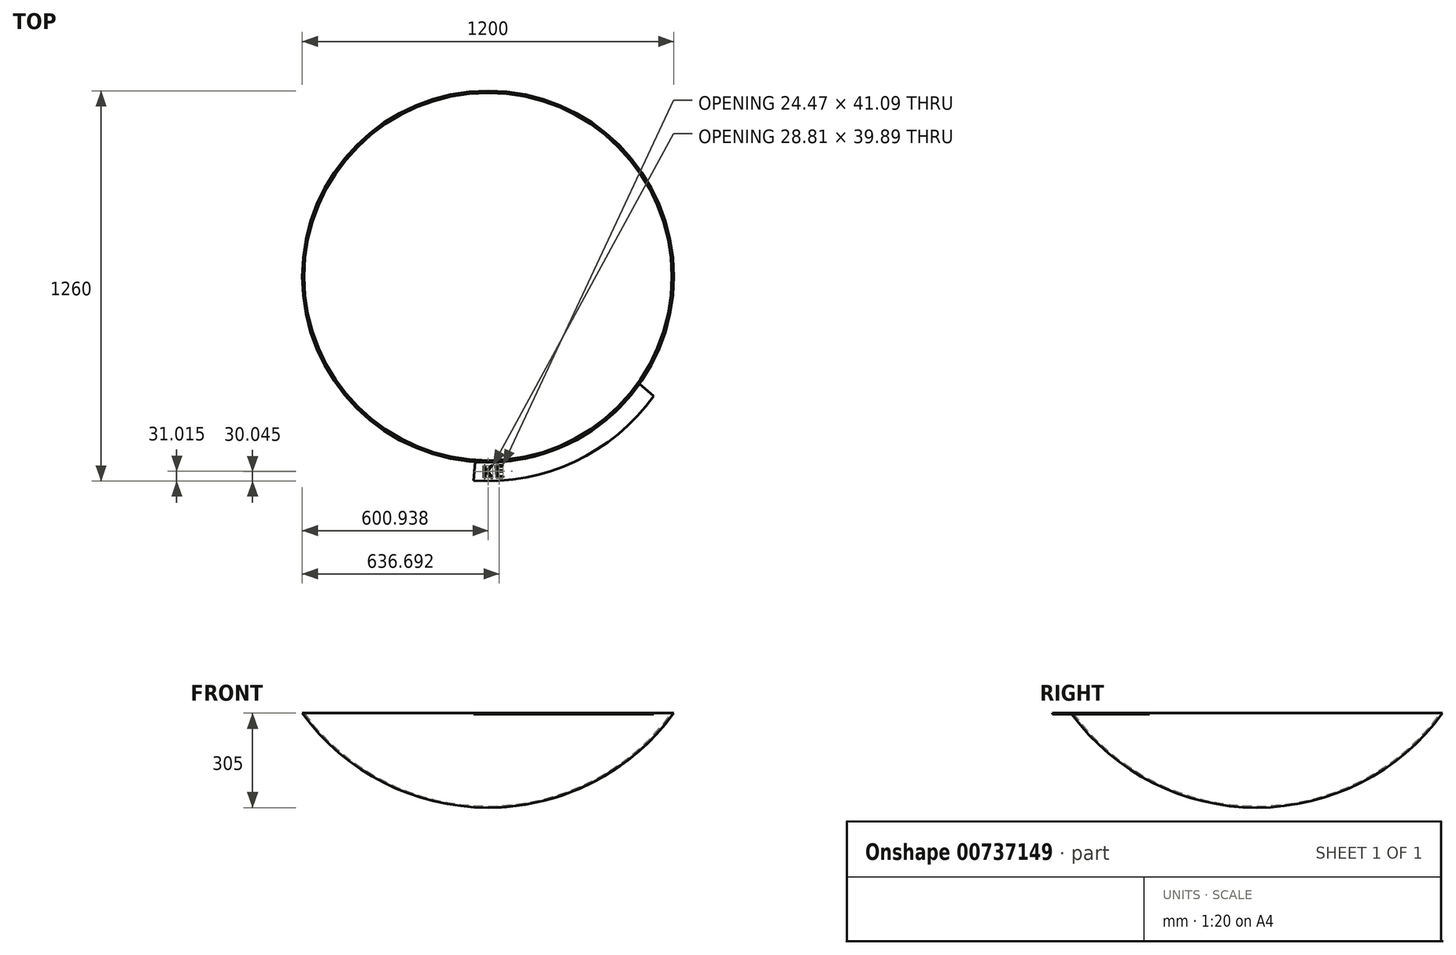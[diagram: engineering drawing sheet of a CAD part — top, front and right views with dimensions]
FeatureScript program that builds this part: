
annotation { "Feature Type Name" : "Feature", "Feature Type Description" : "" }
export const myFeature = defineFeature(function(context is Context, id is Id, definition is map)
    precondition{}
    {
        {
            var Q0;
            Q0=qCreatedBy(makeId("Front.planeOp"),FACE);
            var sketch = newSketch(context, id + "F0", { "sketchPlane" : qUnion([Q0])});
            skArc(sketch, "E0", {"start": v(0, -600) * mm, "mid": v(336.54, -519.37) * mm, "end": v(600, -295) * mm});
            skArc(sketch, "E1.0", {"start": v(0, -595) * mm, "mid": v(332.64, -515.74) * mm, "end": v(593.8, -295) * mm});
            skPoint(sketch, "E2", {"position": v(600, -295) * mm});
            skPoint(sketch, "E3", {"position": v(0, -595) * mm});
            skLineSegment(sketch, "E4.trimOffspring", {"start": v(593.8, -295) * mm, "end": v(600, -295) * mm});
            skLineSegment(sketch, "E5", {"start": v(0, -595) * mm, "end": v(0, -600) * mm});
            skSolve(sketch);
        }
        {
            var Q0;
            Q0 = qSketchRegion(id + "F0", true);
            var Q1;
            Q1=sQuery(id+"F0.wireOp",EDGE,"E5");
            revolve(context, id + "F1", {"surfaceOperationType" : NewSurfaceOperationType.NEW, "entities" : qUnion([Q0]), "axis" : qUnion([Q1]), "revolveType" : RevolveType.FULL});
        }
        {
            var Q0;
            Q0=makeQuery(id+"F1.opRevolve","SWEPT_FACE",FACE,{"disambiguationData":[OSD([sQuery(id+"F0.wireOp",EDGE,"E4.trimOffspring")])]});
            var sketch = newSketch(context, id + "F2", { "sketchPlane" : qUnion([Q0])});
            skCircle(sketch, "E6.0", {"center": v(0, 0) * mm, "radius": 660 * mm});
            skText(sketch, "E7", { "text": "K", "fontName": "OpenSans-Regular.ttf"});
            skLineSegment(sketch, "E8", {"start": v(0, 0) * mm, "end": v(0, -609.67) * mm, "construction": true});
            skText(sketch, "E9", { "text": "E", "fontName": "OpenSans-Regular.ttf"});
            skLineSegment(sketch, "E10", {"start": v(34.61, -608.78) * mm, "end": v(0, 0) * mm, "construction": true});
            skLineSegment(sketch, "E11", {"start": v(-18.95, -649.9) * mm, "end": v(-18.95, -678.41) * mm});
            skLineSegment(sketch, "E12", {"start": v(-41.94, -598.53) * mm, "end": v(-46.69, -658.35) * mm});
            skLineSegment(sketch, "E13", {"start": v(489.46, -347.03) * mm, "end": v(535.74, -385.47) * mm});
            const initialGuessF2  = {"E7": [-0.01895, -0.6499, 1, 1e-05, 0.04023], "E9": [0.02125, -0.64984, 0.99839, 0.05677, 0.04023]};
            skSetInitialGuess(sketch, initialGuessF2);
            skSolve(sketch);
        }
        {
            var Q0;
            Q0=makeQuery(id+"F2.imprint","IMPRINT",FACE,{"disambiguationData":[TD([[makeQuery(id+"F2.imprint","IMPRINT",EDGE,{"derivedFrom":sQuery(id+"F2.wireOp",EDGE,"E7.sketch_text.stroke-0")}),1.0]])]});
            extrude(context, id + "F3", {"entities" : qUnion([Q0]), "oppositeDirection" : true, "depth" : 3 * mm, "offsetDistance" : 25 * mm});
        }
    });
